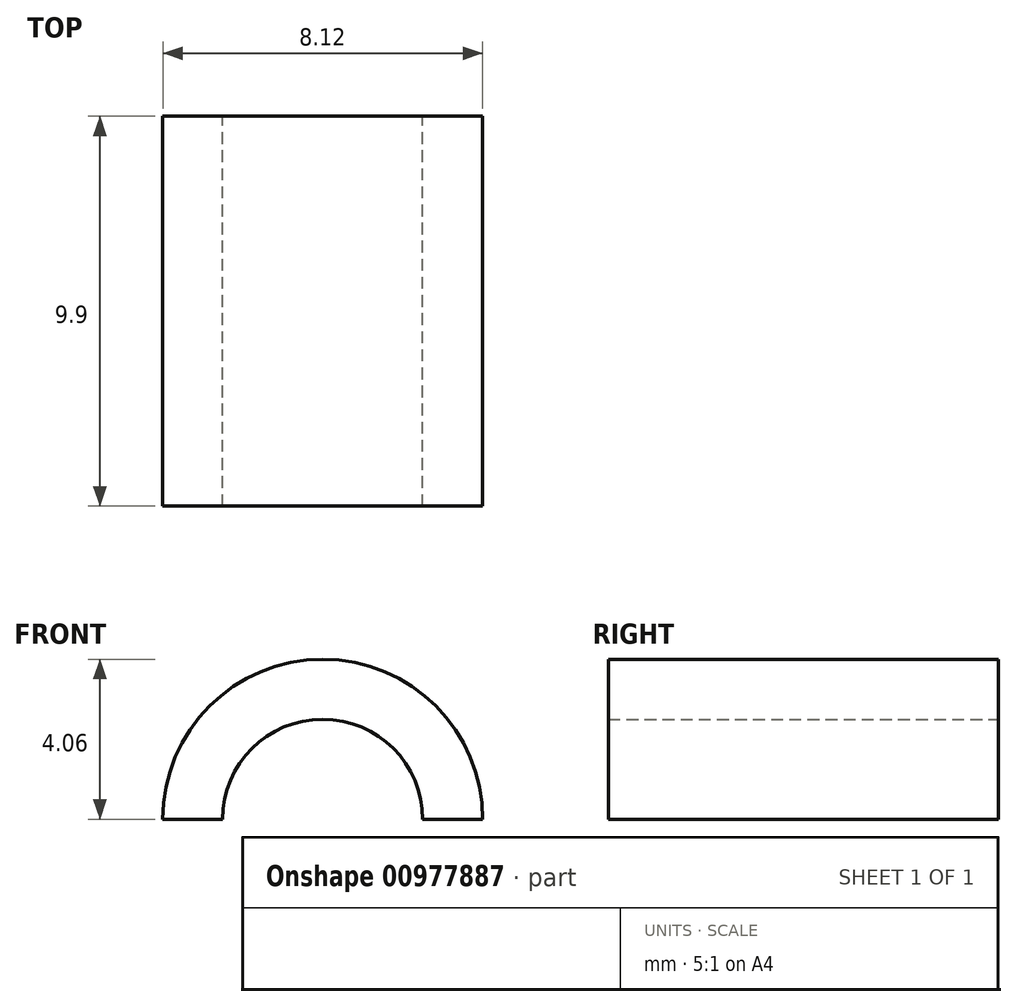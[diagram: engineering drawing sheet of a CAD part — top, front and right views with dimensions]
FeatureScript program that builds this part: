
annotation { "Feature Type Name" : "Feature", "Feature Type Description" : "" }
export const myFeature = defineFeature(function(context is Context, id is Id, definition is map)
    precondition{}
    {
        {
            var Q0;
            Q0=qCreatedBy(makeId("Front.planeOp"),FACE);
            var sketch = newSketch(context, id + "F0", { "sketchPlane" : qUnion([Q0])});
            skArc(sketch, "E0", {"start": v(2.54, 0) * mm, "mid": v(0, 2.54) * mm, "end": v(-2.54, 0) * mm});
            skArc(sketch, "E1", {"start": v(4.06, 0) * mm, "mid": v(0, 4.06) * mm, "end": v(-4.06, 0) * mm});
            skLineSegment(sketch, "E2", {"start": v(2.54, 0) * mm, "end": v(4.06, 0) * mm});
            skLineSegment(sketch, "E3", {"start": v(-2.54, 0) * mm, "end": v(-4.06, 0) * mm});
            skSolve(sketch);
        }
        {
            var Q0;
            Q0=makeQuery(id+"F0.imprint","IMPRINT",FACE,{"disambiguationData":[TD([[makeQuery(id+"F0.imprint","IMPRINT",EDGE,{"derivedFrom":sQuery(id+"F0.wireOp",EDGE,"E0")}),-1.0]])]});
            extrude(context, id + "F1", {"entities" : qUnion([Q0]), "endBound" : BoundingType.SYMMETRIC, "depth" : 9.9 * mm, "offsetDistance" : 25.4 * mm});
        }
    });
